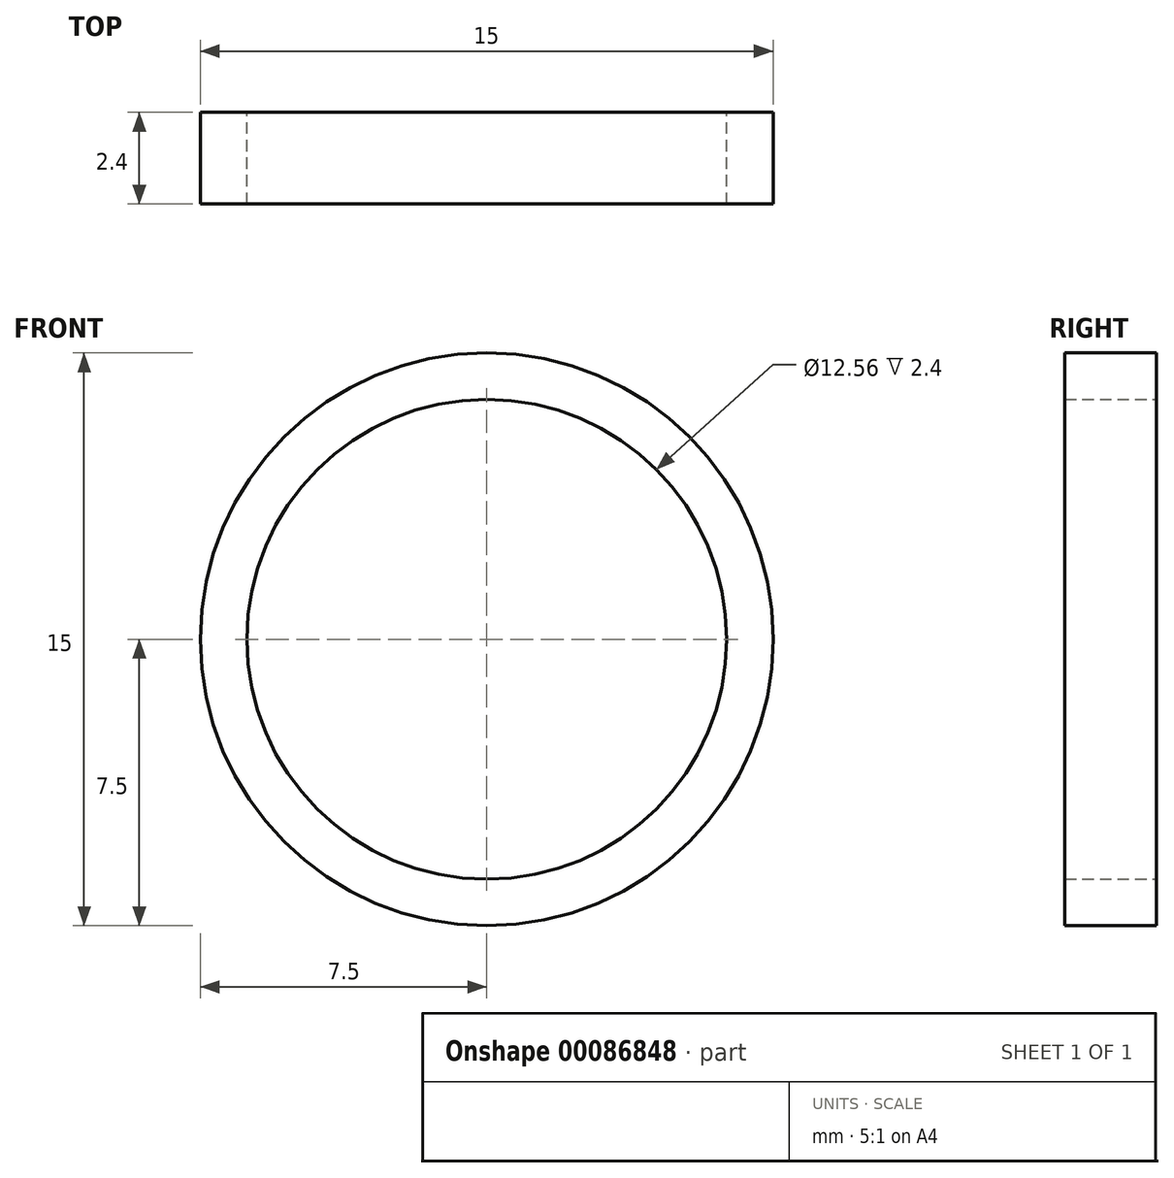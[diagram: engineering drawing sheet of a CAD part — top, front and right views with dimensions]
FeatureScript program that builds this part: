
annotation { "Feature Type Name" : "Feature", "Feature Type Description" : "" }
export const myFeature = defineFeature(function(context is Context, id is Id, definition is map)
    precondition{}
    {
        {
            var Q0;
            Q0=qCreatedBy(makeId("Front.planeOp"),FACE);
            var sketch = newSketch(context, id + "F0", { "sketchPlane" : qUnion([Q0])});
            skCircle(sketch, "E0", {"center": v(0, 0) * mm, "radius": 7.5 * mm});
            skCircle(sketch, "E1", {"center": v(0, 0) * mm, "radius": 6.28 * mm});
            skSolve(sketch);
        }
        {
            var Q0;
            Q0 = qSketchRegion(id + "F0", true);
            var Q1;
            Q1=makeQuery(id+"F0.imprint","IMPRINT",FACE,{"disambiguationData":[TD([[makeQuery(id+"F0.imprint","IMPRINT",EDGE,{"derivedFrom":sQuery(id+"F0.wireOp",EDGE,"E0")}),1.0]])]});
            extrude(context, id + "F1", {"entities" : qUnion([Q0, Q1]), "depth" : 2.4 * mm});
        }
    });
